# Revit family: НЕВАТОМ_Вентилятор VO c защитной решеткой, версия 1
name_source: partatom
category: Оборудование
revit_build: Autodesk Revit 2017 (Build: 20170118_1100(x64)
units: mm (PartAtom-declared; Revit-internal decimal feet)

## family parameters
Всегда вертикально = Да
На основе рабочей плоскости = Нет
Общий = Нет
При загрузке вырезать с полостями = Нет
Размер круглого соединителя = Использовать диаметр
Тип детали = Нормальный
Точка расчета площади = Нет

## types (14) — shared parameters
ADSK_Единица измерения = шт.
ADSK_Завод-изготовитель = НЕВАТОМ
ADSK_Материал наименование = Оцинкованная сталь
Nevatom_URL = https://t.me
Наименование = Вентилятор осевой

## per-type parameters (varying)
| type | A | A/2 | ADSK_Марка | ADSK_Масса | ADSK_Масса_Текст | ADSK_Напряжение | ADSK_Полная мощность | ADSK_Размер_Высота | ADSK_Размер_Длина | ADSK_Размер_Ширина | ADSK_Ток | ADSK_Частота вращения вентилятора | B | C | D | D верх вент | D осн вент | D* | D1 | D1.1 | D2 | D2.1 | H |
| VO 200-4E | 220 мм | 110 мм | VO 200-4Е-02 | 1.9 | 1.9 кг | 230 В | 0 кВт | 250 мм | 250 мм | 126 мм | 0 А | 1460 | 250 мм | 50 мм | 195 мм | 24 мм | 39 мм | 16 мм | 182 мм | 143 мм | 130 мм | 91 мм | 126 мм |
| VO 250-4E | 282 мм | 141 мм | VO 250-4Е-02 | 2.5 | 2.5 кг | 230 В | 0 кВт | 320 мм | 320 мм | 134 мм | 0 А | 1380 | 320 мм | 75 мм | 250 мм | 31 мм | 50 мм | 21 мм | 233 мм | 183 мм | 167 мм | 117 мм | 134 мм |
| VO 300-4Е | 322 мм | 161 мм | VO 300-4Е-02 | 3.2 | 3.2 кг | 230 В | 0 кВт | 360 мм | 360 мм | 158 мм | 0 А | 1370 | 360 мм | 80 мм | 300 мм | 38 мм | 60 мм | 25 мм | 280 мм | 220 мм | 200 мм | 140 мм | 158 мм |
| VO 350-4Е | 375 мм | 188 мм | VO 350-4Е-02 | 4.7 | 4.7 кг | 230 В | 0 кВт | 422 мм | 422 мм | 158 мм | 1 А | 1370 | 422 мм | 80 мм | 350 мм | 44 мм | 70 мм | 29 мм | 327 мм | 257 мм | 233 мм | 163 мм | 158 мм |
| VO 400-4Е | 422 мм | 211 мм | VO 400-4Е-02 | 6.1 | 6.1 кг | 230 В | 0 кВт | 470 мм | 470 мм | 171 мм | 1 А | 1350 | 470 мм | 90 мм | 391 мм | 49 мм | 78 мм | 33 мм | 365 мм | 287 мм | 261 мм | 182 мм | 171 мм |
| VO 450-4E | 475 мм | 238 мм | VO 450-4Е-02 | 6.9 | 6.9 кг | 230 В | 0 кВт | 522 мм | 522 мм | 183 мм | 1 А | 1380 | 522 мм | 90 мм | 446 мм | 56 мм | 89 мм | 37 мм | 416 мм | 327 мм | 297 мм | 208 мм | 183 мм |
| VO 400-4D | 422 мм | 211 мм | VO 400-4D-02 | 6.1 | 6.1 кг | 380 В | 0 кВт | 470 мм | 470 мм | 171 мм | 0 А | 1380 | 470 мм | 90 мм | 391 мм | 49 мм | 78 мм | 33 мм | 365 мм | 287 мм | 261 мм | 182 мм | 171 мм |
| VO 450-4D | 475 мм | 238 мм | VO 450-4D-02 | 6.9 | 6.9 кг | 380 В | 0 кВт | 522 мм | 522 мм | 183 мм | 1 А | 1400 | 522 мм | 90 мм | 446 мм | 56 мм | 89 мм | 37 мм | 416 мм | 327 мм | 297 мм | 208 мм | 183 мм |
| VO 500-4E | 525 мм | 263 мм | VO 500-4E-02 | 9.5 | 9.5 кг | 230 В | 0 кВт | 570 мм | 570 мм | 186 мм | 2 А | 1320 | 570 мм | 90 мм | 499 мм | 62 мм | 100 мм | 42 мм | 466 мм | 366 мм | 333 мм | 233 мм | 186 мм |
| VO 500-4D | 525 мм | 263 мм | VO 500-4D-02 | 9.5 | 9.5 кг | 380 В | 0 кВт | 570 мм | 570 мм | 186 мм | 1 А | 1320 | 570 мм | 90 мм | 499 мм | 62 мм | 100 мм | 42 мм | 466 мм | 366 мм | 333 мм | 233 мм | 186 мм |
| VO 560-4E | 575 мм | 288 мм | VO 560-4E-02 | 10.5 | 10.5 кг | 230 В | 1 кВт | 624 мм | 624 мм | 201 мм | 2 А | 1310 | 624 мм | 100 мм | 553 мм | 69 мм | 111 мм | 46 мм | 516 мм | 406 мм | 369 мм | 258 мм | 201 мм |
| VO 560-4D | 575 мм | 288 мм | VO 560-4D-02 | 10.5 | 10.5 кг | 380 В | 1 кВт | 624 мм | 624 мм | 201 мм | 1 А | 1300 | 624 мм | 100 мм | 553 мм | 69 мм | 111 мм | 46 мм | 516 мм | 406 мм | 369 мм | 258 мм | 201 мм |
| VO 630-4E | 680 мм | 340 мм | VO 630-4E-02 | 15 | 15.0 кг | 230 В | 1 кВт | 750 мм | 750 мм | 221 мм | 4 А | 1315 | 750 мм | 100 мм | 628 мм | 79 мм | 126 мм | 52 мм | 586 мм | 461 мм | 419 мм | 293 мм | 221 мм |
| VO 630-4D | 680 мм | 340 мм | VO 630-6D-02 | 15 | 15.0 кг | 380 В | 1 кВт | 750 мм | 750 мм | 221 мм | 2 А | 1365 | 750 мм | 100 мм | 628 мм | 79 мм | 126 мм | 52 мм | 586 мм | 461 мм | 419 мм | 293 мм | 221 мм |
